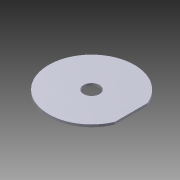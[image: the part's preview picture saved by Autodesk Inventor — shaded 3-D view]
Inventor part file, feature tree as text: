
AUTODESK INVENTOR PART (.ipt)
format: ipt  version: 2013 (Build 170138000, 138)  size: 81,408 bytes
history: native  units: mm
features: extrude x1, sketch x1
ambient origin geometry x8: Origin, YZ Plane, XZ Plane, XY Plane, X Axis, Y Axis, Z Axis, Center Point
feature tree (2):
  extrude  "Extrusion3"  Depth=20.0mm
  sketch  "Sketch1"  dims[d0=108.0mm d1=20.0mm d12=50.0mm d14=54.0mm d17=3.0mm d18=0.0mm]
